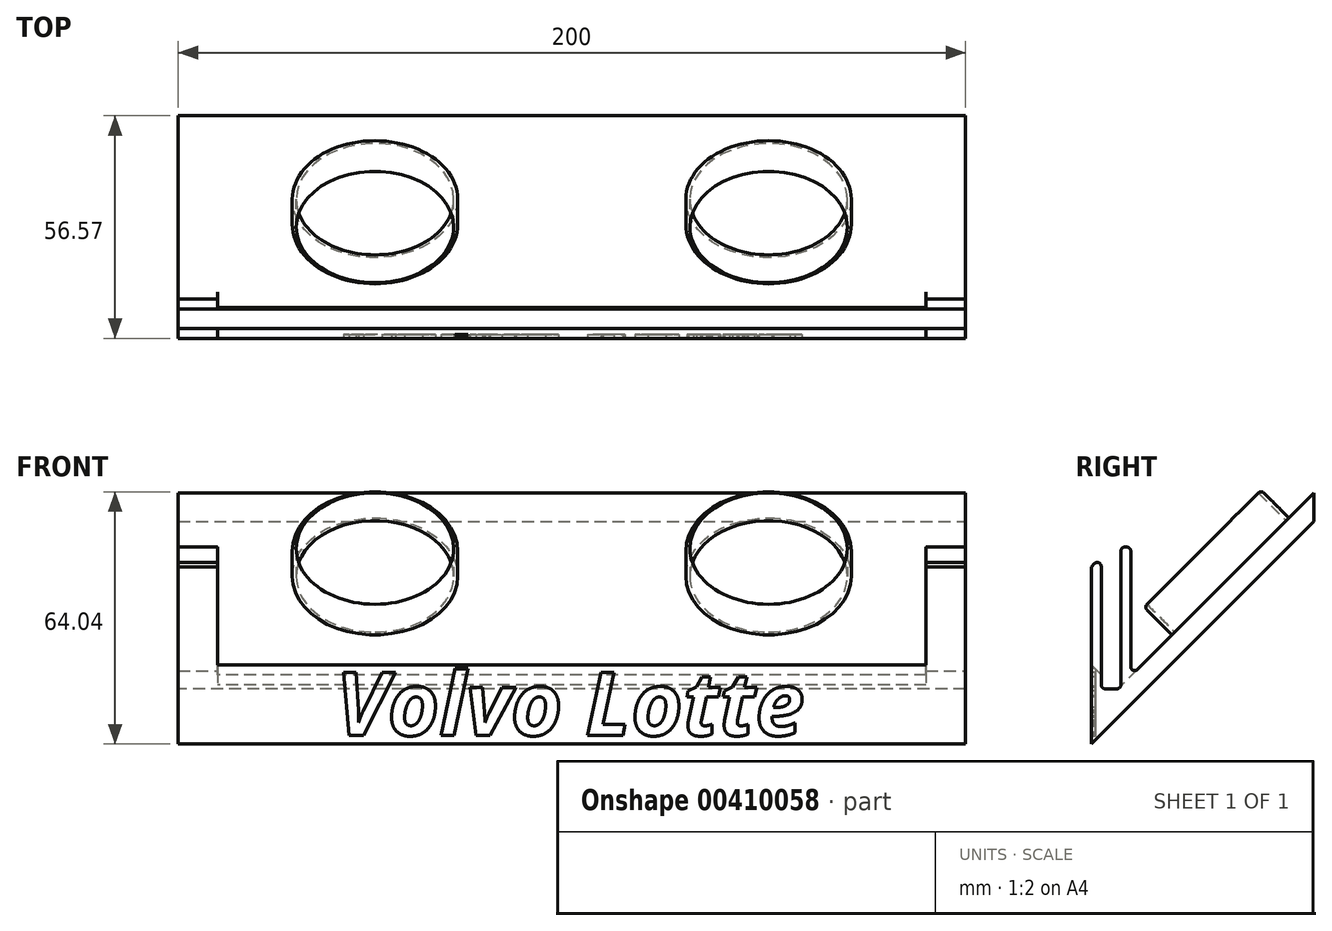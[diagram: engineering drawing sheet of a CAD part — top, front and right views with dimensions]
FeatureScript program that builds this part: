
annotation { "Feature Type Name" : "Feature", "Feature Type Description" : "" }
export const myFeature = defineFeature(function(context is Context, id is Id, definition is map)
    precondition{}
    {
        {
            var Q0;
            Q0=qCreatedBy(makeId("Front.planeOp"),FACE);
            var sketch = newSketch(context, id + "F0", { "sketchPlane" : qUnion([Q0])});
            skLineSegment(sketch, "E0.bottom", {"start": v(-100, 25) * mm, "end": v(100, 25) * mm});
            skLineSegment(sketch, "E0.top", {"start": v(-100, -25) * mm, "end": v(100, -25) * mm});
            skLineSegment(sketch, "E0.left", {"start": v(-100, 25) * mm, "end": v(-100, -25) * mm});
            skLineSegment(sketch, "E0.right", {"start": v(100, 25) * mm, "end": v(100, -25) * mm});
            skPoint(sketch, "E0.middle", {"position": v(0, 0) * mm});
            skSolve(sketch);
        }
        {
            var Q0;
            Q0 = qSketchRegion(id + "F0", true);
            extrude(context, id + "F1", {"entities" : qUnion([Q0]), "depth" : 5 * mm});
        }
        {
            var Q0;
            Q0=makeQuery(id+"F1.opExtrude","SWEPT_FACE",FACE,{"disambiguationData":[OSD([sQuery(id+"F0.wireOp",EDGE,"E0.right")])]});
            var sketch = newSketch(context, id + "F2", { "sketchPlane" : qUnion([Q0])});
            skLineSegment(sketch, "E1", {"start": v(0, 25) * mm, "end": v(-5, 20) * mm});
            skLineSegment(sketch, "E2", {"start": v(-5, -25) * mm, "end": v(0, -20) * mm});
            skSolve(sketch);
        }
        {
            var Q0;
            {var subQ0=sQuery(id+"F2.wireOp",EDGE,"E1");Q0=makeQuery(id+"F2.imprint","IMPRINT",FACE,{"disambiguationData":[TD([[makeQuery(id+"F2.imprint","IMPRINT",EDGE,{"derivedFrom":subQ0}),-1.0]])]});}
            var Q1;
            {var subQ0=sQuery(id+"F2.wireOp",EDGE,"E2");Q1=makeQuery(id+"F2.imprint","IMPRINT",FACE,{"disambiguationData":[TD([[makeQuery(id+"F2.imprint","IMPRINT",EDGE,{"derivedFrom":subQ0}),-1.0]])]});}
            extrude(context, id + "F3", {"entities" : qUnion([Q0, Q1]), "operationType" : NewBodyOperationType.REMOVE, "oppositeDirection" : true, "depth" : 200 * mm});
        }
        {
            var Q0;
            Q0=makeQuery(id+"F1.opExtrude","SWEPT_FACE",FACE,{"disambiguationData":[OSD([sQuery(id+"F0.wireOp",EDGE,"E0.right")])]});
            var sketch = newSketch(context, id + "F4", { "sketchPlane" : qUnion([Q0])});
            skLineSegment(sketch, "E3", {"start": v(-5, -25) * mm, "end": v(51.57, 31.57) * mm});
            skLineSegment(sketch, "E4", {"start": v(-5, -17.82) * mm, "end": v(51.57, 38.75) * mm});
            skLineSegment(sketch, "E5", {"start": v(51.57, 38.75) * mm, "end": v(51.57, 31.57) * mm});
            skSolve(sketch);
        }
        {
            var Q0;
            Q0 = qSketchRegion(id + "F4", true);
            var Q1;
            {var subQ3=sQuery(id+"F4.wireOp",EDGE,"E5");Q1=makeQuery(id+"F4.imprint","IMPRINT",FACE,{"disambiguationData":[TD([[makeQuery(id+"F4.imprint","IMPRINT",EDGE,{"derivedFrom":subQ3}),-1.0]])]});}
            extrude(context, id + "F5", {"entities" : qUnion([Q0, Q1]), "operationType" : NewBodyOperationType.ADD, "oppositeDirection" : true, "depth" : 200 * mm});
        }
        {
            var Q0;
            Q0=makeQuery(id+"F1.opExtrude","CAP_FACE",FACE,{"disambiguationData":[OSD([sQuery(id+"F0.wireOp",EDGE,"E0.bottom"),sQuery(id+"F0.wireOp",EDGE,"E0.top"),sQuery(id+"F0.wireOp",EDGE,"E0.left"),sQuery(id+"F0.wireOp",EDGE,"E0.right")])],"isStart":false});
            var sketch = newSketch(context, id + "F6", { "sketchPlane" : qUnion([Q0])});
            skLineSegment(sketch, "E6.bottom", {"start": v(-90, 20) * mm, "end": v(90, 20) * mm});
            skLineSegment(sketch, "E6.top", {"start": v(-90, -5) * mm, "end": v(90, -5) * mm});
            skLineSegment(sketch, "E6.left", {"start": v(-90, 20) * mm, "end": v(-90, -5) * mm});
            skLineSegment(sketch, "E6.right", {"start": v(90, 20) * mm, "end": v(90, -5) * mm});
            skSolve(sketch);
        }
        {
            var Q0;
            Q0=makeQuery(id+"F3.boolean.opBoolean","COPY",FACE,{"derivedFrom":makeQuery(id+"F3.opExtrude","SWEPT_FACE",FACE,{"disambiguationData":[OSD([sQuery(id+"F2.wireOp",EDGE,"E1")])]})});
            var sketch = newSketch(context, id + "F7", { "sketchPlane" : qUnion([Q0])});
            skLineSegment(sketch, "E7", {"start": v(-90, 10.6) * mm, "end": v(-90, 17.68) * mm});
            skLineSegment(sketch, "E8", {"start": v(90, 10.6) * mm, "end": v(90, 17.68) * mm});
            skSolve(sketch);
        }
        {
            var Q0;
            {var subQ0=sQuery(id+"F7.wireOp",EDGE,"E7");Q0=makeQuery(id+"F7.imprint","IMPRINT",FACE,{"disambiguationData":[TD([[makeQuery(id+"F7.imprint","IMPRINT",EDGE,{"derivedFrom":subQ0}),-1.0]])]});}
            var Q1;
            Q1=makeQuery(id+"F6.imprint","IMPRINT",FACE,{"disambiguationData":[TD([[makeQuery(id+"F6.imprint","IMPRINT",EDGE,{"derivedFrom":sQuery(id+"F6.wireOp",EDGE,"E6.bottom")}),-1.0]])]});
            extrude(context, id + "F8", {"entities" : qUnion([Q0, Q1]), "operationType" : NewBodyOperationType.REMOVE, "oppositeDirection" : true, "depth" : 9 * mm});
        }
        {
            var Q0;
            Q0=makeQuery(id+"F1.opExtrude","CAP_FACE",FACE,{"disambiguationData":[OSD([sQuery(id+"F0.wireOp",EDGE,"E0.bottom"),sQuery(id+"F0.wireOp",EDGE,"E0.top"),sQuery(id+"F0.wireOp",EDGE,"E0.left"),sQuery(id+"F0.wireOp",EDGE,"E0.right")])],"isStart":true});
            extrude(context, id + "F9", {"entities" : qUnion([Q0]), "operationType" : NewBodyOperationType.ADD, "depth" : 5 * mm});
        }
        {
            var Q0;
            {var subQ0=sQuery(id+"F0.wireOp",EDGE,"E0.left");Q0=makeQuery(id+"F9.boolean.opBoolean","MERGE",FACE,{"derivedFrom":[makeQuery(id+"F5.boolean.opBoolean","MERGE",FACE,{"derivedFrom":[makeQuery(id+"F1.opExtrude","SWEPT_FACE",FACE,{"disambiguationData":[OSD([subQ0])]}),makeQuery(id+"F5.opExtrude","CAP_FACE",FACE,{"disambiguationData":[OSD([sQuery(id+"F0.wireOp",EDGE,"E0.right"),sQuery(id+"F4.wireOp",EDGE,"E3"),sQuery(id+"F4.wireOp",EDGE,"E4"),sQuery(id+"F4.wireOp",EDGE,"E5")])],"isStart":false})]}),makeQuery(id+"F9.opExtrude","SWEPT_FACE",FACE,{"disambiguationData":[OSD([subQ0])]})]});}
            var sketch = newSketch(context, id + "F10", { "sketchPlane" : qUnion([Q0])});
            skPoint(sketch, "E9.oppositeSnap0", {"position": v(-2.5, 25) * mm});
            skLineSegment(sketch, "E9.bottom", {"start": v(2.5, -11) * mm, "end": v(-2.5, -11) * mm});
            skLineSegment(sketch, "E9.top", {"start": v(2.5, 29) * mm, "end": v(-2.5, 29) * mm});
            skLineSegment(sketch, "E9.left", {"start": v(2.5, -11) * mm, "end": v(2.5, 29) * mm});
            skLineSegment(sketch, "E9.right", {"start": v(-2.5, -11) * mm, "end": v(-2.5, 29) * mm});
            skSolve(sketch);
        }
        {
            var Q0;
            Q0 = qSketchRegion(id + "F10", true);
            extrude(context, id + "F11", {"entities" : qUnion([Q0]), "operationType" : NewBodyOperationType.REMOVE, "oppositeDirection" : true, "depth" : 200 * mm});
        }
        {
            var Q0;
            Q0=makeQuery(id+"F5.opExtrude","SWEPT_FACE",FACE,{"disambiguationData":[OSD([sQuery(id+"F4.wireOp",EDGE,"E4")])]});
            var sketch = newSketch(context, id + "F12", { "sketchPlane" : qUnion([Q0])});
            skPoint(sketch, "E10", {"position": v(0, 33.86) * mm});
            skLineSegment(sketch, "E11", {"start": v(-100, 33.86) * mm, "end": v(100, 33.86) * mm, "construction": true});
            skPoint(sketch, "E12", {"position": v(-50, 33.86) * mm});
            skPoint(sketch, "E13", {"position": v(50, 33.86) * mm});
            skCircle(sketch, "E14", {"center": v(-50, 33.86) * mm, "radius": 20 * mm});
            skCircle(sketch, "E15", {"center": v(50, 33.86) * mm, "radius": 20 * mm});
            skCircle(sketch, "E16", {"center": v(-50, 33.86) * mm, "radius": 21 * mm});
            skCircle(sketch, "E17", {"center": v(50, 33.86) * mm, "radius": 21 * mm});
            skSolve(sketch);
        }
        {
            var Q0;
            Q0 = qSketchRegion(id + "F12", true);
            extrude(context, id + "F13", {"entities" : qUnion([Q0]), "operationType" : NewBodyOperationType.ADD, "depth" : 10 * mm});
        }
        {
            var Q0;
            Q0=makeQuery(id+"F13.opExtrude","CAP_EDGE",EDGE,{"disambiguationData":[OSD([sQuery(id+"F12.wireOp",EDGE,"E16")])],"isStart":false});
            var Q1;
            Q1=makeQuery(id+"F13.opExtrude","CAP_EDGE",EDGE,{"disambiguationData":[OSD([sQuery(id+"F12.wireOp",EDGE,"E17")])],"isStart":false});
            var Q2;
            Q2=makeQuery(id+"F9.boolean.opBoolean","INTERSECT",EDGE,{"disambiguationData":[OD(1.0)],"derivedFrom":[makeQuery(id+"F5.opExtrude","SWEPT_FACE",FACE,{"disambiguationData":[OSD([sQuery(id+"F4.wireOp",EDGE,"E4")])]}),makeQuery(id+"F9.opExtrude","CAP_FACE",FACE,{"disambiguationData":[OSD([sQuery(id+"F0.wireOp",EDGE,"E0.bottom"),sQuery(id+"F0.wireOp",EDGE,"E0.top"),sQuery(id+"F0.wireOp",EDGE,"E0.left"),sQuery(id+"F0.wireOp",EDGE,"E0.right")])],"isStart":false})]});
            var Q3;
            Q3=makeQuery(id+"F11.boolean.opBoolean","COPY",EDGE,{"derivedFrom":makeQuery(id+"F11.opExtrude","SWEPT_EDGE",EDGE,{"disambiguationData":[OSD([sQuery(id+"F10.wireOp",EDGE,"E9.bottom"),sQuery(id+"F10.wireOp",EDGE,"E9.left")])]})});
            var Q4;
            Q4=makeQuery(id+"F11.boolean.opBoolean","COPY",EDGE,{"derivedFrom":makeQuery(id+"F11.opExtrude","SWEPT_EDGE",EDGE,{"disambiguationData":[OSD([sQuery(id+"F10.wireOp",EDGE,"E9.bottom"),sQuery(id+"F10.wireOp",EDGE,"E9.right")])]})});
            var Q5;
            Q5=makeQuery(id+"F9.boolean.opBoolean","INTERSECT",EDGE,{"disambiguationData":[OD(0.0)],"derivedFrom":[makeQuery(id+"F5.opExtrude","SWEPT_FACE",FACE,{"disambiguationData":[OSD([sQuery(id+"F4.wireOp",EDGE,"E4")])]}),makeQuery(id+"F9.opExtrude","CAP_FACE",FACE,{"disambiguationData":[OSD([sQuery(id+"F0.wireOp",EDGE,"E0.bottom"),sQuery(id+"F0.wireOp",EDGE,"E0.top"),sQuery(id+"F0.wireOp",EDGE,"E0.left"),sQuery(id+"F0.wireOp",EDGE,"E0.right")])],"isStart":false})]});
            var Q6;
            {var subQ0=sQuery(id+"F0.wireOp",EDGE,"E0.right");var subQ1=sQuery(id+"F2.wireOp",EDGE,"E1");var subQ2=sQuery(id+"F0.wireOp",EDGE,"E0.bottom");Q6=makeQuery(id+"F11.boolean.opBoolean","INTERSECT",EDGE,{"derivedFrom":[makeQuery(id+"F9.opExtrude","SWEPT_FACE",FACE,{"disambiguationData":[OSD([subQ2,subQ0,subQ1]),TDD([makeQuery(id+"F8.boolean.opBoolean","SPLIT",EDGE,{"disambiguationData":[TD([makeQuery(id+"F1.opExtrude","SWEPT_FACE",FACE,{"disambiguationData":[OSD([subQ0])]})])],"derivedFrom":makeQuery(id+"F3.boolean.opBoolean","MERGE",EDGE,{"derivedFrom":[makeQuery(id+"F1.opExtrude","CAP_EDGE",EDGE,{"disambiguationData":[OSD([subQ2])],"isStart":true}),makeQuery(id+"F3.opExtrude","SWEPT_EDGE",EDGE,{"disambiguationData":[OSD([subQ2,subQ0,subQ1])]})]})})])]}),makeQuery(id+"F11.opExtrude","SWEPT_FACE",FACE,{"disambiguationData":[OSD([sQuery(id+"F10.wireOp",EDGE,"E9.right")])]})]});}
            var Q7;
            {var subQ0=sQuery(id+"F0.wireOp",EDGE,"E0.right");var subQ1=sQuery(id+"F2.wireOp",EDGE,"E1");var subQ2=sQuery(id+"F0.wireOp",EDGE,"E0.left");var subQ3=sQuery(id+"F0.wireOp",EDGE,"E0.bottom");Q7=makeQuery(id+"F11.boolean.opBoolean","INTERSECT",EDGE,{"derivedFrom":[makeQuery(id+"F9.opExtrude","SWEPT_FACE",FACE,{"disambiguationData":[OSD([subQ3,subQ0,subQ1]),TDD([makeQuery(id+"F8.boolean.opBoolean","SPLIT",EDGE,{"disambiguationData":[TD([makeQuery(id+"F1.opExtrude","SWEPT_FACE",FACE,{"disambiguationData":[OSD([subQ2])]})])],"derivedFrom":makeQuery(id+"F3.boolean.opBoolean","MERGE",EDGE,{"derivedFrom":[makeQuery(id+"F1.opExtrude","CAP_EDGE",EDGE,{"disambiguationData":[OSD([subQ3])],"isStart":true}),makeQuery(id+"F3.opExtrude","SWEPT_EDGE",EDGE,{"disambiguationData":[OSD([subQ3,subQ0,subQ1])]})]})})])]}),makeQuery(id+"F11.opExtrude","SWEPT_FACE",FACE,{"disambiguationData":[OSD([sQuery(id+"F10.wireOp",EDGE,"E9.right")])]})]});}
            var Q8;
            {var subQ1=sQuery(id+"F0.wireOp",EDGE,"E0.left");Q8=makeQuery(id+"F11.boolean.opBoolean","INTERSECT",EDGE,{"derivedFrom":[makeQuery(id+"F8.boolean.opBoolean","SPLIT",FACE,{"disambiguationData":[TD([makeQuery(id+"F1.opExtrude","SWEPT_FACE",FACE,{"disambiguationData":[OSD([subQ1])]})])],"derivedFrom":makeQuery(id+"F3.boolean.opBoolean","COPY",FACE,{"derivedFrom":makeQuery(id+"F3.opExtrude","SWEPT_FACE",FACE,{"disambiguationData":[OSD([sQuery(id+"F2.wireOp",EDGE,"E1")])]})})}),makeQuery(id+"F11.opExtrude","SWEPT_FACE",FACE,{"disambiguationData":[OSD([sQuery(id+"F10.wireOp",EDGE,"E9.left")])]})]});}
            var Q9;
            {var subQ0=sQuery(id+"F0.wireOp",EDGE,"E0.right");Q9=makeQuery(id+"F11.boolean.opBoolean","INTERSECT",EDGE,{"derivedFrom":[makeQuery(id+"F8.boolean.opBoolean","SPLIT",FACE,{"disambiguationData":[TD([makeQuery(id+"F1.opExtrude","SWEPT_FACE",FACE,{"disambiguationData":[OSD([subQ0])]})])],"derivedFrom":makeQuery(id+"F3.boolean.opBoolean","COPY",FACE,{"derivedFrom":makeQuery(id+"F3.opExtrude","SWEPT_FACE",FACE,{"disambiguationData":[OSD([sQuery(id+"F2.wireOp",EDGE,"E1")])]})})}),makeQuery(id+"F11.opExtrude","SWEPT_FACE",FACE,{"disambiguationData":[OSD([sQuery(id+"F10.wireOp",EDGE,"E9.left")])]})]});}
            var Q10;
            {var subQ0=sQuery(id+"F0.wireOp",EDGE,"E0.right");var subQ1=sQuery(id+"F2.wireOp",EDGE,"E1");var subQ2=sQuery(id+"F0.wireOp",EDGE,"E0.left");Q10=makeQuery(id+"F8.boolean.opBoolean","SPLIT",EDGE,{"disambiguationData":[TD([makeQuery(id+"F1.opExtrude","SWEPT_FACE",FACE,{"disambiguationData":[OSD([subQ2])]})])],"derivedFrom":makeQuery(id+"F3.boolean.opBoolean","COPY",EDGE,{"derivedFrom":makeQuery(id+"F3.opExtrude","SWEPT_EDGE",EDGE,{"disambiguationData":[OSD([subQ0,subQ1])]})})});}
            var Q11;
            {var subQ0=sQuery(id+"F0.wireOp",EDGE,"E0.right");var subQ1=sQuery(id+"F2.wireOp",EDGE,"E1");var subQ2=sQuery(id+"F0.wireOp",EDGE,"E0.left");var subQ3=sQuery(id+"F0.wireOp",EDGE,"E0.bottom");Q11=makeQuery(id+"F9.opExtrude","CAP_EDGE",EDGE,{"disambiguationData":[OSD([subQ3,subQ0,subQ1]),TDD([makeQuery(id+"F8.boolean.opBoolean","SPLIT",EDGE,{"disambiguationData":[TD([makeQuery(id+"F1.opExtrude","SWEPT_FACE",FACE,{"disambiguationData":[OSD([subQ2])]})])],"derivedFrom":makeQuery(id+"F3.boolean.opBoolean","MERGE",EDGE,{"derivedFrom":[makeQuery(id+"F1.opExtrude","CAP_EDGE",EDGE,{"disambiguationData":[OSD([subQ3])],"isStart":true}),makeQuery(id+"F3.opExtrude","SWEPT_EDGE",EDGE,{"disambiguationData":[OSD([subQ3,subQ0,subQ1])]})]})})])],"isStart":false});}
            var Q12;
            {var subQ0=sQuery(id+"F0.wireOp",EDGE,"E0.right");var subQ1=sQuery(id+"F2.wireOp",EDGE,"E1");var subQ2=sQuery(id+"F0.wireOp",EDGE,"E0.bottom");Q12=makeQuery(id+"F9.opExtrude","CAP_EDGE",EDGE,{"disambiguationData":[OSD([subQ2,subQ0,subQ1]),TDD([makeQuery(id+"F8.boolean.opBoolean","SPLIT",EDGE,{"disambiguationData":[TD([makeQuery(id+"F1.opExtrude","SWEPT_FACE",FACE,{"disambiguationData":[OSD([subQ0])]})])],"derivedFrom":makeQuery(id+"F3.boolean.opBoolean","MERGE",EDGE,{"derivedFrom":[makeQuery(id+"F1.opExtrude","CAP_EDGE",EDGE,{"disambiguationData":[OSD([subQ2])],"isStart":true}),makeQuery(id+"F3.opExtrude","SWEPT_EDGE",EDGE,{"disambiguationData":[OSD([subQ2,subQ0,subQ1])]})]})})])],"isStart":false});}
            var Q13;
            {var subQ0=sQuery(id+"F0.wireOp",EDGE,"E0.right");var subQ1=sQuery(id+"F2.wireOp",EDGE,"E1");Q13=makeQuery(id+"F8.boolean.opBoolean","SPLIT",EDGE,{"disambiguationData":[TD([makeQuery(id+"F1.opExtrude","SWEPT_FACE",FACE,{"disambiguationData":[OSD([subQ0])]})])],"derivedFrom":makeQuery(id+"F3.boolean.opBoolean","COPY",EDGE,{"derivedFrom":makeQuery(id+"F3.opExtrude","SWEPT_EDGE",EDGE,{"disambiguationData":[OSD([subQ0,subQ1])]})})});}
            var Q14;
            Q14=makeQuery(id+"F13.opExtrude","CAP_EDGE",EDGE,{"disambiguationData":[OSD([sQuery(id+"F12.wireOp",EDGE,"E16")])],"isStart":true});
            var Q15;
            Q15=makeQuery(id+"F13.opExtrude","CAP_EDGE",EDGE,{"disambiguationData":[OSD([sQuery(id+"F12.wireOp",EDGE,"E17")])],"isStart":true});
            fillet(context, id + "F14", {"entities" : qUnion([Q0, Q1, Q2, Q3, Q4, Q5, Q6, Q7, Q8, Q9, Q10, Q11, Q12, Q13, Q14, Q15]), "radius" : 1 * mm, "tangentPropagation" : true, "allowEdgeOverflow" : false});
        }
        {
            var Q0;
            Q0=makeQuery(id+"F1.opExtrude","CAP_FACE",FACE,{"disambiguationData":[OSD([sQuery(id+"F0.wireOp",EDGE,"E0.bottom"),sQuery(id+"F0.wireOp",EDGE,"E0.top"),sQuery(id+"F0.wireOp",EDGE,"E0.left"),sQuery(id+"F0.wireOp",EDGE,"E0.right")])],"isStart":false});
            var sketch = newSketch(context, id + "F15", { "sketchPlane" : qUnion([Q0])});
            skText(sketch, "E18", { "text": "Volvo Lotte ", "fontName": "OpenSans-BoldItalic.ttf"});
            const initialGuessF15  = {"E18": [-0.06, -0.02286, 1, 0, 0.01615]};
            skSetInitialGuess(sketch, initialGuessF15);
            skSolve(sketch);
        }
        {
            var Q0;
            Q0 = qSketchRegion(id + "F15", true);
            extrude(context, id + "F16", {"entities" : qUnion([Q0]), "operationType" : NewBodyOperationType.REMOVE, "oppositeDirection" : true, "depth" : 1 * mm});
        }
    });
